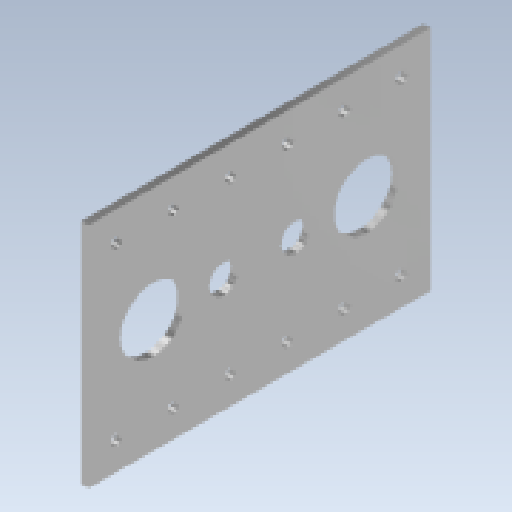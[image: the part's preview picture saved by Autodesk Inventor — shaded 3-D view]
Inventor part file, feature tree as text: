
AUTODESK INVENTOR PART (.ipt)
format: ipt  version: 2023 (Build 270158000, 158)  size: 149,504 bytes
history: native  units: in
note: dims shown in document units (in); Inventor stores cm internally (conversion verified against a paired STEP export)
features: extrude x1, sketch x1
ambient origin geometry x8: Origin, YZ Plane, XZ Plane, XY Plane, X Axis, Y Axis, Z Axis, Center Point
bodies: Solid1 (feature_tree)
feature tree (2):
  extrude  "Extrusion1"  Depth=6.0in
  sketch  "Sketch1"  dims[d0=4.0in d1=6.0in d2=1.125in d3=0.5in d4=0.5in d5=1.125in d6=1.25in d7=1.25in d8=1.25in d9=0.2087in d10=0.5in d11=0.5in d12=2.3622in d14=1.0in d15=0.7874in d17=3.0in d20=0.125in d21=0.0in d22=0.5in d23=0.0344in d24=0.5in d25=0.0344in]
